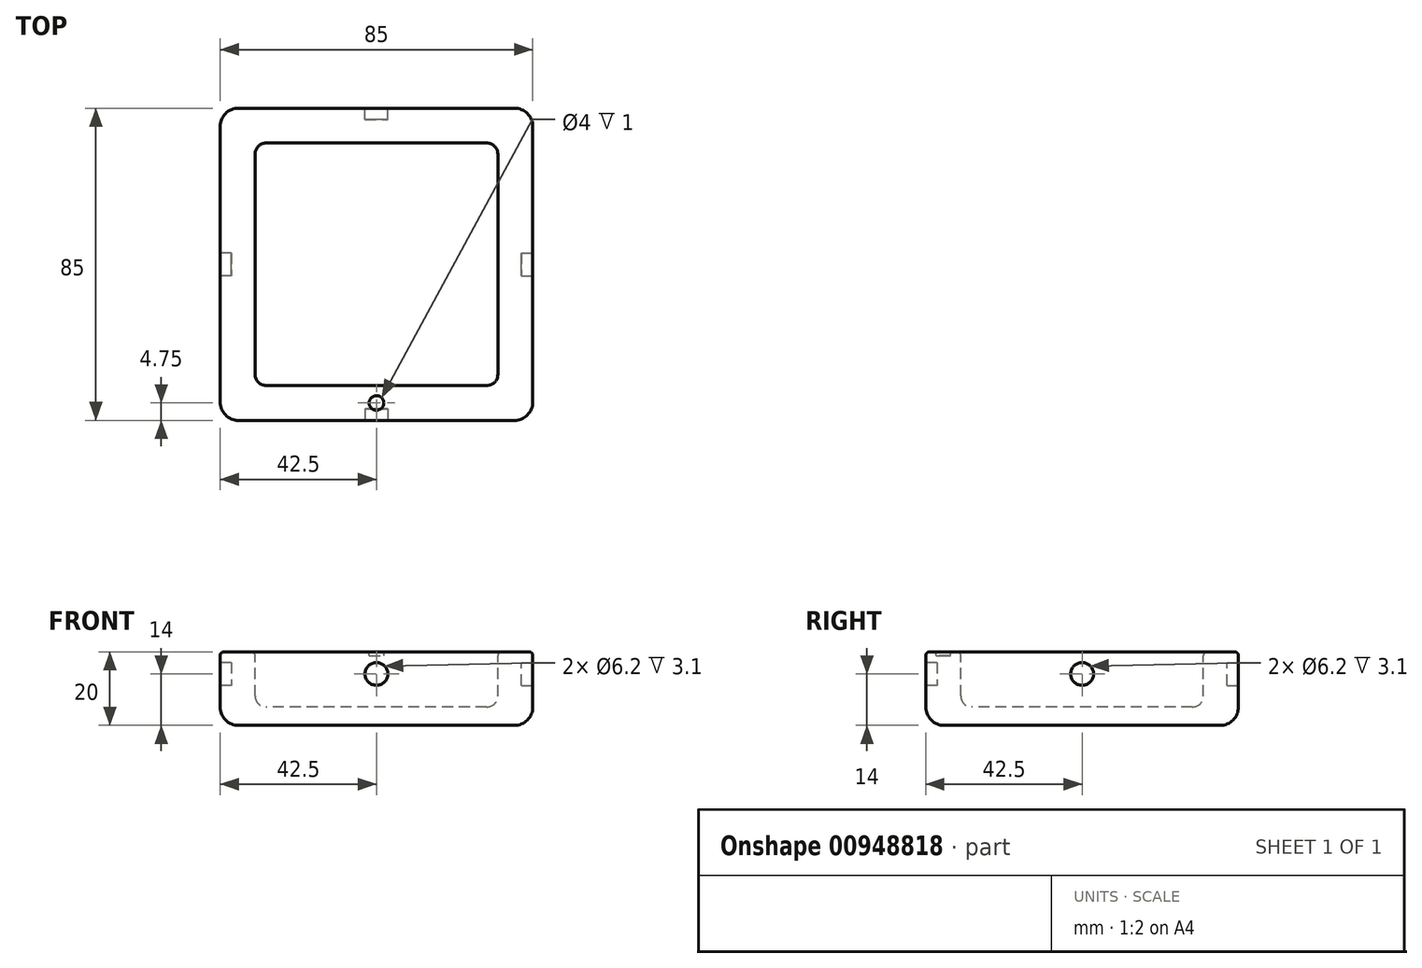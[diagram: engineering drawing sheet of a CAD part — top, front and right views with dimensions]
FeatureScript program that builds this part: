
annotation { "Feature Type Name" : "Feature", "Feature Type Description" : "" }
export const myFeature = defineFeature(function(context is Context, id is Id, definition is map)
    precondition{}
    {
        {
            var Q0;
            Q0=qCreatedBy(makeId("Top.planeOp"),FACE);
            var sketch = newSketch(context, id + "F0", { "sketchPlane" : qUnion([Q0])});
            skLineSegment(sketch, "E0.bottom", {"start": v(-42.5, 42.5) * mm, "end": v(42.5, 42.5) * mm});
            skLineSegment(sketch, "E0.top", {"start": v(-42.5, -42.5) * mm, "end": v(42.5, -42.5) * mm});
            skLineSegment(sketch, "E0.left", {"start": v(-42.5, 42.5) * mm, "end": v(-42.5, -42.5) * mm});
            skLineSegment(sketch, "E0.right", {"start": v(42.5, 42.5) * mm, "end": v(42.5, -42.5) * mm});
            skLineSegment(sketch, "E1.bottom", {"start": v(-30, 33) * mm, "end": v(30, 33) * mm});
            skLineSegment(sketch, "E1.top", {"start": v(-30, -33) * mm, "end": v(30, -33) * mm});
            skLineSegment(sketch, "E1.left", {"start": v(-33, 30) * mm, "end": v(-33, -30) * mm});
            skLineSegment(sketch, "E1.right", {"start": v(33, 30) * mm, "end": v(33, -30) * mm});
            skLineSegment(sketch, "E2.direction1", {"start": v(-33, -33) * mm, "end": v(-8.24, -33) * mm, "construction": true});
            skPoint(sketch, "E3.visualSharp", {"position": v(-33, 33) * mm});
            skArc(sketch, "E3.filletArc", {"start": v(-30, 33) * mm, "mid": v(-32.12, 32.12) * mm, "end": v(-33, 30) * mm});
            skPoint(sketch, "E4.visualSharp", {"position": v(33, 33) * mm});
            skArc(sketch, "E4.filletArc", {"start": v(33, 30) * mm, "mid": v(32.12, 32.12) * mm, "end": v(30, 33) * mm});
            skPoint(sketch, "E5.visualSharp", {"position": v(33, -33) * mm});
            skArc(sketch, "E5.filletArc", {"start": v(30, -33) * mm, "mid": v(32.12, -32.12) * mm, "end": v(33, -30) * mm});
            skPoint(sketch, "E6.visualSharp", {"position": v(-33, -33) * mm});
            skArc(sketch, "E6.filletArc", {"start": v(-33, -30) * mm, "mid": v(-32.12, -32.12) * mm, "end": v(-30, -33) * mm});
            skLineSegment(sketch, "E7.direction1", {"start": v(-33, -33) * mm, "end": v(-6.5, -33) * mm, "construction": true});
            skLineSegment(sketch, "E8", {"start": v(-42.5, 0) * mm, "end": v(42.5, 0) * mm, "construction": true});
            skLineSegment(sketch, "E9", {"start": v(0, -42.5) * mm, "end": v(0, 42.5) * mm, "construction": true});
            skCircle(sketch, "E10", {"center": v(0, -37.75) * mm, "radius": 2 * mm});
            skSolve(sketch);
        }
        {
            var Q0;
            Q0=makeQuery(id+"F0.imprint","IMPRINT",FACE,{"disambiguationData":[TD([[makeQuery(id+"F0.imprint","IMPRINT",EDGE,{"derivedFrom":sQuery(id+"F0.wireOp",EDGE,"E1.bottom")}),-1.0]])]});
            var Q1;
            Q1=makeQuery(id+"F0.imprint","IMPRINT",FACE,{"disambiguationData":[TD([[makeQuery(id+"F0.imprint","IMPRINT",EDGE,{"derivedFrom":sQuery(id+"F0.wireOp",EDGE,"E0.bottom")}),-1.0]])]});
            var Q2;
            Q2=makeQuery(id+"F0.imprint","IMPRINT",FACE,{"disambiguationData":[TD([[makeQuery(id+"F0.imprint","IMPRINT",EDGE,{"derivedFrom":sQuery(id+"F0.wireOp",EDGE,"E2.0.2.0")}),1.0]])]});
            var Q3;
            Q3=makeQuery(id+"F0.imprint","IMPRINT",FACE,{"disambiguationData":[TD([[makeQuery(id+"F0.imprint","IMPRINT",EDGE,{"derivedFrom":sQuery(id+"F0.wireOp",EDGE,"E2.0.3.0")}),1.0]])]});
            var Q4;
            Q4=makeQuery(id+"F0.imprint","IMPRINT",FACE,{"disambiguationData":[TD([[makeQuery(id+"F0.imprint","IMPRINT",EDGE,{"derivedFrom":sQuery(id+"F0.wireOp",EDGE,"E2.0.1.0")}),1.0]])]});
            var Q5;
            Q5=makeQuery(id+"F0.imprint","IMPRINT",FACE,{"disambiguationData":[TD([[makeQuery(id+"F0.imprint","IMPRINT",EDGE,{"derivedFrom":sQuery(id+"F0.wireOp",EDGE,"E7.0.1.2")}),1.0]])]});
            var Q6;
            Q6=makeQuery(id+"F0.imprint","IMPRINT",FACE,{"disambiguationData":[TD([[makeQuery(id+"F0.imprint","IMPRINT",EDGE,{"derivedFrom":sQuery(id+"F0.wireOp",EDGE,"E7.0.2.2")}),1.0]])]});
            var Q7;
            Q7=makeQuery(id+"F0.imprint","IMPRINT",FACE,{"disambiguationData":[TD([[makeQuery(id+"F0.imprint","IMPRINT",EDGE,{"derivedFrom":sQuery(id+"F0.wireOp",EDGE,"E7.0.3.2")}),1.0]])]});
            var Q8;
            Q8=makeQuery(id+"F0.imprint","IMPRINT",FACE,{"disambiguationData":[TD([[makeQuery(id+"F0.imprint","IMPRINT",EDGE,{"derivedFrom":sQuery(id+"F0.wireOp",EDGE,"E10")}),1.0]])]});
            extrude(context, id + "F1", {"entities" : qUnion([Q0, Q1, Q2, Q3, Q4, Q5, Q6, Q7, Q8]), "depth" : 20 * mm, "offsetDistance" : 25 * mm});
        }
        {
            var Q0;
            Q0=makeQuery(id+"F0.imprint","IMPRINT",FACE,{"disambiguationData":[TD([[makeQuery(id+"F0.imprint","IMPRINT",EDGE,{"derivedFrom":sQuery(id+"F0.wireOp",EDGE,"E1.bottom")}),-1.0]])]});
            var Q1;
            Q1=makeQuery(id+"F0.imprint","IMPRINT",FACE,{"disambiguationData":[TD([[makeQuery(id+"F0.imprint","IMPRINT",EDGE,{"derivedFrom":sQuery(id+"F0.wireOp",EDGE,"E2.0.1.0")}),1.0]])]});
            var Q2;
            Q2=makeQuery(id+"F0.imprint","IMPRINT",FACE,{"disambiguationData":[TD([[makeQuery(id+"F0.imprint","IMPRINT",EDGE,{"derivedFrom":sQuery(id+"F0.wireOp",EDGE,"E2.0.2.0")}),1.0]])]});
            var Q3;
            Q3=makeQuery(id+"F0.imprint","IMPRINT",FACE,{"disambiguationData":[TD([[makeQuery(id+"F0.imprint","IMPRINT",EDGE,{"derivedFrom":sQuery(id+"F0.wireOp",EDGE,"E2.0.3.0")}),1.0]])]});
            var Q4;
            Q4=makeQuery(id+"F0.imprint","IMPRINT",FACE,{"disambiguationData":[TD([[makeQuery(id+"F0.imprint","IMPRINT",EDGE,{"derivedFrom":sQuery(id+"F0.wireOp",EDGE,"E7.0.1.2")}),1.0]])]});
            var Q5;
            Q5=makeQuery(id+"F0.imprint","IMPRINT",FACE,{"disambiguationData":[TD([[makeQuery(id+"F0.imprint","IMPRINT",EDGE,{"derivedFrom":sQuery(id+"F0.wireOp",EDGE,"E7.0.2.2")}),1.0]])]});
            var Q6;
            Q6=makeQuery(id+"F0.imprint","IMPRINT",FACE,{"disambiguationData":[TD([[makeQuery(id+"F0.imprint","IMPRINT",EDGE,{"derivedFrom":sQuery(id+"F0.wireOp",EDGE,"E7.0.3.2")}),1.0]])]});
            extrude(context, id + "F2", {"entities" : qUnion([Q0, Q1, Q2, Q3, Q4, Q5, Q6]), "operationType" : NewBodyOperationType.REMOVE, "depth" : 15 * mm, "offsetDistance" : 25 * mm});
        }
        {
            var Q0;
            Q0=makeQuery(id+"F1.opExtrude","CAP_FACE",FACE,{"disambiguationData":[OSD([sQuery(id+"F0.wireOp",EDGE,"E0.bottom"),sQuery(id+"F0.wireOp",EDGE,"E0.top"),sQuery(id+"F0.wireOp",EDGE,"E0.left"),sQuery(id+"F0.wireOp",EDGE,"E0.right")])],"isStart":false});
            var Q1;
            Q1=makeQuery(id+"F1.opExtrude","SWEPT_EDGE",EDGE,{"disambiguationData":[OSD([sQuery(id+"F0.wireOp",EDGE,"E0.bottom"),sQuery(id+"F0.wireOp",EDGE,"E0.right")])]});
            var Q2;
            Q2=makeQuery(id+"F1.opExtrude","SWEPT_EDGE",EDGE,{"disambiguationData":[OSD([sQuery(id+"F0.wireOp",EDGE,"E0.bottom"),sQuery(id+"F0.wireOp",EDGE,"E0.left")])]});
            var Q3;
            Q3=makeQuery(id+"F1.opExtrude","SWEPT_EDGE",EDGE,{"disambiguationData":[OSD([sQuery(id+"F0.wireOp",EDGE,"E0.top"),sQuery(id+"F0.wireOp",EDGE,"E0.left")])]});
            var Q4;
            Q4=makeQuery(id+"F1.opExtrude","SWEPT_EDGE",EDGE,{"disambiguationData":[OSD([sQuery(id+"F0.wireOp",EDGE,"E0.top"),sQuery(id+"F0.wireOp",EDGE,"E0.right")])]});
            fillet(context, id + "F3", {"entities" : qUnion([Q0, Q1, Q2, Q3, Q4]), "radius" : 5 * mm, "tangentPropagation" : true, "allowEdgeOverflow" : false});
        }
        {
            var Q0;
            Q0=makeQuery(id+"F2.boolean.opBoolean","COPY",FACE,{"derivedFrom":makeQuery(id+"F2.opExtrude","CAP_FACE",FACE,{"disambiguationData":[OSD([sQuery(id+"F0.wireOp",EDGE,"E1.bottom"),sQuery(id+"F0.wireOp",EDGE,"E1.top"),sQuery(id+"F0.wireOp",EDGE,"E1.left"),sQuery(id+"F0.wireOp",EDGE,"E1.right"),sQuery(id+"F0.wireOp",EDGE,"E3.filletArc"),sQuery(id+"F0.wireOp",EDGE,"E4.filletArc"),sQuery(id+"F0.wireOp",EDGE,"E5.filletArc"),sQuery(id+"F0.wireOp",EDGE,"E6.filletArc")])],"isStart":false})});
            var Q1;
            Q1=makeQuery(id+"F2.boolean.opBoolean","COPY",FACE,{"derivedFrom":makeQuery(id+"F2.opExtrude","CAP_FACE",FACE,{"disambiguationData":[OSD([sQuery(id+"F0.wireOp",EDGE,"E7.0.1.2"),sQuery(id+"F0.wireOp",EDGE,"E7.0.1.4"),sQuery(id+"F0.wireOp",EDGE,"E7.0.1.5"),sQuery(id+"F0.wireOp",EDGE,"E7.0.1.6"),sQuery(id+"F0.wireOp",EDGE,"E7.0.1.7"),sQuery(id+"F0.wireOp",EDGE,"E7.0.1.9"),sQuery(id+"F0.wireOp",EDGE,"E7.0.1.11"),sQuery(id+"F0.wireOp",EDGE,"E7.0.1.12")])],"isStart":false})});
            var Q2;
            Q2=makeQuery(id+"F2.boolean.opBoolean","COPY",FACE,{"derivedFrom":makeQuery(id+"F2.opExtrude","CAP_FACE",FACE,{"disambiguationData":[OSD([sQuery(id+"F0.wireOp",EDGE,"E7.0.2.2"),sQuery(id+"F0.wireOp",EDGE,"E7.0.2.4"),sQuery(id+"F0.wireOp",EDGE,"E7.0.2.5"),sQuery(id+"F0.wireOp",EDGE,"E7.0.2.6"),sQuery(id+"F0.wireOp",EDGE,"E7.0.2.7"),sQuery(id+"F0.wireOp",EDGE,"E7.0.2.9"),sQuery(id+"F0.wireOp",EDGE,"E7.0.2.11"),sQuery(id+"F0.wireOp",EDGE,"E7.0.2.12")])],"isStart":false})});
            var Q3;
            Q3=makeQuery(id+"F2.boolean.opBoolean","COPY",FACE,{"derivedFrom":makeQuery(id+"F2.opExtrude","CAP_FACE",FACE,{"disambiguationData":[OSD([sQuery(id+"F0.wireOp",EDGE,"E7.0.3.2"),sQuery(id+"F0.wireOp",EDGE,"E7.0.3.4"),sQuery(id+"F0.wireOp",EDGE,"E7.0.3.5"),sQuery(id+"F0.wireOp",EDGE,"E7.0.3.6"),sQuery(id+"F0.wireOp",EDGE,"E7.0.3.7"),sQuery(id+"F0.wireOp",EDGE,"E7.0.3.9"),sQuery(id+"F0.wireOp",EDGE,"E7.0.3.11"),sQuery(id+"F0.wireOp",EDGE,"E7.0.3.12")])],"isStart":false})});
            fillet(context, id + "F4", {"entities" : qUnion([Q0, Q1, Q2, Q3]), "radius" : 3 * mm, "tangentPropagation" : true, "allowEdgeOverflow" : false});
        }
        {
            var Q0;
            Q0=makeQuery(id+"F1.opExtrude","CAP_FACE",FACE,{"disambiguationData":[OSD([sQuery(id+"F0.wireOp",EDGE,"E0.bottom"),sQuery(id+"F0.wireOp",EDGE,"E0.top"),sQuery(id+"F0.wireOp",EDGE,"E0.left"),sQuery(id+"F0.wireOp",EDGE,"E0.right")])],"isStart":true});
            fillet(context, id + "F5", {"entities" : qUnion([Q0]), "radius" : 1 * mm, "tangentPropagation" : true, "allowEdgeOverflow" : false});
        }
        {
            var Q0;
            Q0=makeQuery(id+"F1.opExtrude","SWEPT_FACE",FACE,{"disambiguationData":[OSD([sQuery(id+"F0.wireOp",EDGE,"E0.top")])]});
            var sketch = newSketch(context, id + "F6", { "sketchPlane" : qUnion([Q0])});
            skCircle(sketch, "E11", {"center": v(0, 6) * mm, "radius": 3.1 * mm});
            skSolve(sketch);
        }
        {
            var Q0;
            Q0=makeQuery(id+"F6.imprint","IMPRINT",FACE,{"disambiguationData":[TD([[makeQuery(id+"F6.imprint","IMPRINT",EDGE,{"derivedFrom":sQuery(id+"F6.wireOp",EDGE,"E11")}),1.0]])]});
            extrude(context, id + "F7", {"entities" : qUnion([Q0]), "operationType" : NewBodyOperationType.REMOVE, "oppositeDirection" : true, "depth" : 3.1 * mm, "offsetDistance" : 25 * mm});
        }
        {
            var Q0;
            Q0=makeQuery(id+"F1.opExtrude","SWEPT_FACE",FACE,{"disambiguationData":[OSD([sQuery(id+"F0.wireOp",EDGE,"E0.bottom")])]});
            var sketch = newSketch(context, id + "F8", { "sketchPlane" : qUnion([Q0])});
            skCircle(sketch, "E12", {"center": v(0, 6) * mm, "radius": 3.1 * mm});
            skSolve(sketch);
        }
        {
            var Q0;
            Q0=makeQuery(id+"F8.imprint","IMPRINT",FACE,{"disambiguationData":[TD([[makeQuery(id+"F8.imprint","IMPRINT",EDGE,{"derivedFrom":sQuery(id+"F8.wireOp",EDGE,"E12")}),1.0]])]});
            extrude(context, id + "F9", {"entities" : qUnion([Q0]), "operationType" : NewBodyOperationType.REMOVE, "oppositeDirection" : true, "depth" : 3.1 * mm, "offsetDistance" : 25 * mm});
        }
        {
            var Q0;
            Q0=makeQuery(id+"F1.opExtrude","SWEPT_FACE",FACE,{"disambiguationData":[OSD([sQuery(id+"F0.wireOp",EDGE,"E0.left")])]});
            var sketch = newSketch(context, id + "F10", { "sketchPlane" : qUnion([Q0])});
            skCircle(sketch, "E13", {"center": v(0, 6) * mm, "radius": 3.1 * mm});
            skSolve(sketch);
        }
        {
            var Q0;
            Q0=makeQuery(id+"F10.imprint","IMPRINT",FACE,{"disambiguationData":[TD([[makeQuery(id+"F10.imprint","IMPRINT",EDGE,{"derivedFrom":sQuery(id+"F10.wireOp",EDGE,"E13")}),1.0]])]});
            extrude(context, id + "F11", {"entities" : qUnion([Q0]), "operationType" : NewBodyOperationType.REMOVE, "oppositeDirection" : true, "depth" : 3.1 * mm, "offsetDistance" : 25 * mm});
        }
        {
            var Q0;
            Q0=makeQuery(id+"F1.opExtrude","SWEPT_FACE",FACE,{"disambiguationData":[OSD([sQuery(id+"F0.wireOp",EDGE,"E0.right")])]});
            var sketch = newSketch(context, id + "F12", { "sketchPlane" : qUnion([Q0])});
            skCircle(sketch, "E14", {"center": v(0, 6) * mm, "radius": 3.1 * mm});
            skSolve(sketch);
        }
        {
            var Q0;
            Q0=makeQuery(id+"F12.imprint","IMPRINT",FACE,{"disambiguationData":[TD([[makeQuery(id+"F12.imprint","IMPRINT",EDGE,{"derivedFrom":sQuery(id+"F12.wireOp",EDGE,"E14")}),1.0]])]});
            extrude(context, id + "F13", {"entities" : qUnion([Q0]), "operationType" : NewBodyOperationType.REMOVE, "oppositeDirection" : true, "depth" : 3.1 * mm, "offsetDistance" : 25 * mm});
        }
        {
            var Q0;
            Q0=makeQuery(id+"F0.imprint","IMPRINT",FACE,{"disambiguationData":[TD([[makeQuery(id+"F0.imprint","IMPRINT",EDGE,{"derivedFrom":sQuery(id+"F0.wireOp",EDGE,"E10")}),1.0]])]});
            var Q1;
            Q1=sQuery(id+"F0.wireOp",EDGE,"E10");
            extrude(context, id + "F14", {"entities" : qUnion([Q0]), "operationType" : NewBodyOperationType.REMOVE, "surfaceEntities" : qUnion([Q1]), "depth" : 1 * mm, "offsetDistance" : 25 * mm});
        }
        {
            var Q0;
            Q0=makeQuery(id+"F1.opExtrude","SWEPT_BODY",BODY,{"disambiguationData":[OSD([sQuery(id+"F0.wireOp",EDGE,"E0.bottom"),sQuery(id+"F0.wireOp",EDGE,"E0.top"),sQuery(id+"F0.wireOp",EDGE,"E0.left"),sQuery(id+"F0.wireOp",EDGE,"E0.right")])]});
            var Q1;
            Q1=sQuery(id+"F0.wireOp",EDGE,"E9");
            var Q2;
            Q2=sQuery(id+"F0.wireOp",EDGE,"E9");
            transform(context, id + "F15", {"entities" : qUnion([Q0]), "transformType" : TransformType.ROTATION, "transformAxis" : qUnion([Q2]), "angle" : 180 * degree, "makeCopy" : false});
        }
    });
